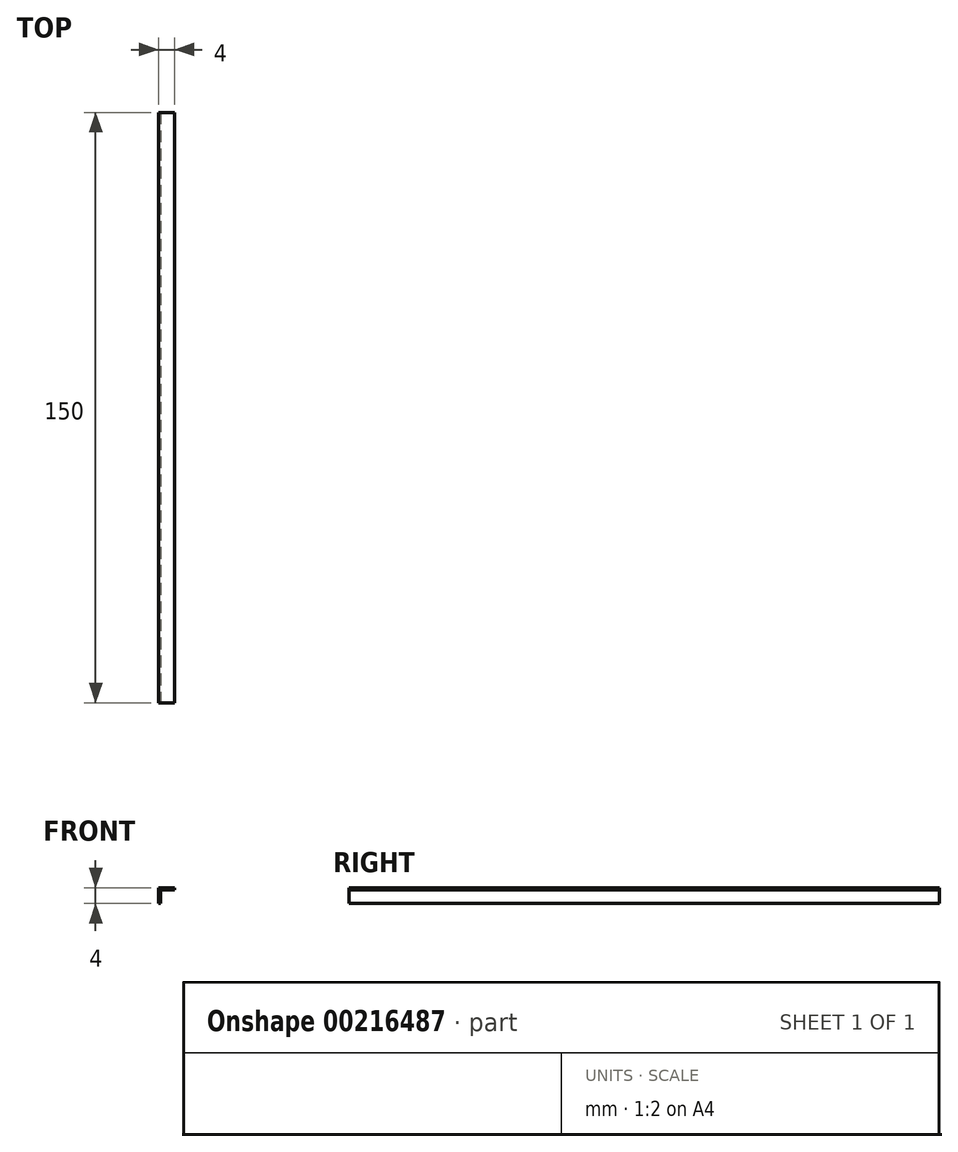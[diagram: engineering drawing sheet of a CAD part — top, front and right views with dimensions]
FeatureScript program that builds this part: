
annotation { "Feature Type Name" : "Feature", "Feature Type Description" : "" }
export const myFeature = defineFeature(function(context is Context, id is Id, definition is map)
    precondition{}
    {
        {
            var Q0;
            Q0=qCreatedBy(makeId("Front.planeOp"),FACE);
            var sketch = newSketch(context, id + "F0", { "sketchPlane" : qUnion([Q0])});
            skLineSegment(sketch, "E0.bottom", {"start": v(0, 0) * mm, "end": v(0.5, 0) * mm});
            skLineSegment(sketch, "E0.left", {"start": v(0, 0) * mm, "end": v(0, 4) * mm});
            skLineSegment(sketch, "E0.right", {"start": v(0.5, 0) * mm, "end": v(0.5, 3.5) * mm});
            skLineSegment(sketch, "E1.top", {"start": v(0.5, 3.5) * mm, "end": v(4, 3.5) * mm});
            skLineSegment(sketch, "E1.right", {"start": v(4, 4) * mm, "end": v(4, 3.5) * mm});
            skLineSegment(sketch, "E2", {"start": v(0, 4) * mm, "end": v(4, 4) * mm});
            skSolve(sketch);
        }
        {
            var Q0;
            Q0 = qSketchRegion(id + "F0", true);
            var Q1;
            Q1 = qConstructionFilter(qBodyType(qCreatedBy(id + "F0" ,EDGE), BodyType.WIRE), ConstructionObject.NO);
            extrude(context, id + "F1", {"entities" : qUnion([Q0]), "surfaceEntities" : qUnion([Q1]), "oppositeDirection" : true, "depth" : 150 * mm});
        }
    });
